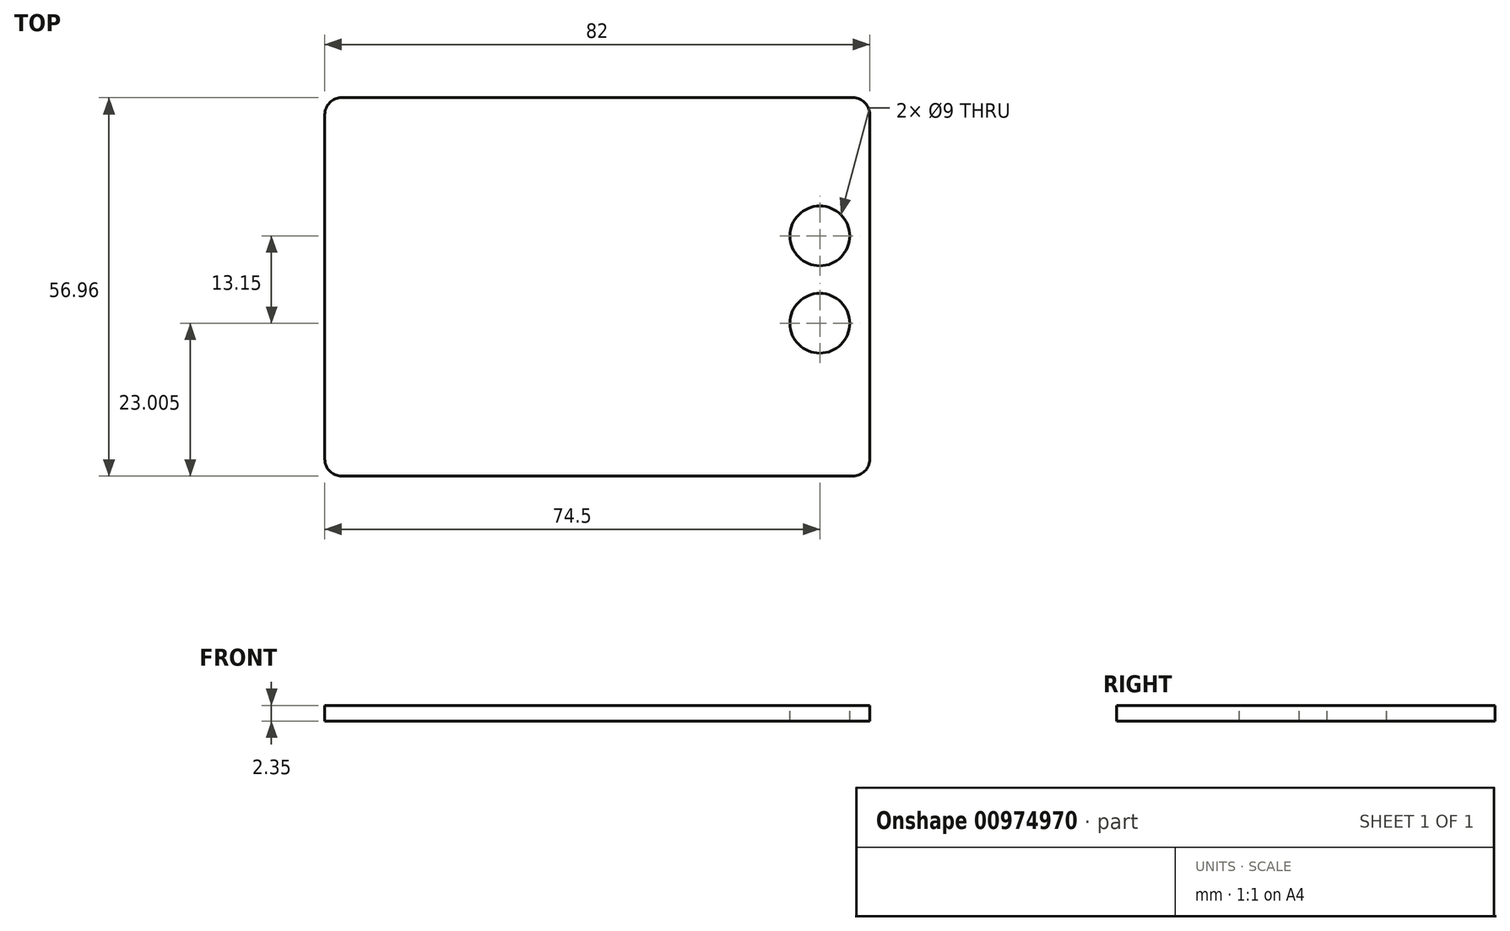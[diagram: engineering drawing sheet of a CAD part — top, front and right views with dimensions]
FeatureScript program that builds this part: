
annotation { "Feature Type Name" : "Feature", "Feature Type Description" : "" }
export const myFeature = defineFeature(function(context is Context, id is Id, definition is map)
    precondition{}
    {
        {
            var Q0;
            Q0=qCreatedBy(makeId("Top.planeOp"),FACE);
            var sketch = newSketch(context, id + "F0", { "sketchPlane" : qUnion([Q0])});
            skLineSegment(sketch, "E0.bottom", {"start": v(-41, 28.47) * mm, "end": v(41, 28.47) * mm});
            skLineSegment(sketch, "E0.top", {"start": v(-41, -28.48) * mm, "end": v(41, -28.48) * mm});
            skLineSegment(sketch, "E0.left", {"start": v(-41, 28.47) * mm, "end": v(-41, -28.47) * mm});
            skLineSegment(sketch, "E0.right", {"start": v(41, 28.47) * mm, "end": v(41, -28.47) * mm});
            skPoint(sketch, "E0.middle", {"position": v(0, 0) * mm});
            skSolve(sketch);
        }
        {
            var Q0;
            Q0 = qSketchRegion(id + "F0", true);
            extrude(context, id + "F1", {"entities" : qUnion([Q0]), "depth" : 2.35 * mm, "offsetDistance" : 25.4 * mm});
        }
        {
            var Q0;
            Q0=makeQuery(id+"F1.opExtrude","SWEPT_EDGE",EDGE,{"disambiguationData":[OSD([sQuery(id+"F0.wireOp",EDGE,"E0.bottom"),sQuery(id+"F0.wireOp",EDGE,"E0.left")])]});
            var Q1;
            Q1=makeQuery(id+"F1.opExtrude","SWEPT_EDGE",EDGE,{"disambiguationData":[OSD([sQuery(id+"F0.wireOp",EDGE,"E0.top"),sQuery(id+"F0.wireOp",EDGE,"E0.left")])]});
            var Q2;
            Q2=makeQuery(id+"F1.opExtrude","SWEPT_EDGE",EDGE,{"disambiguationData":[OSD([sQuery(id+"F0.wireOp",EDGE,"E0.bottom"),sQuery(id+"F0.wireOp",EDGE,"E0.right")])]});
            var Q3;
            Q3=makeQuery(id+"F1.opExtrude","SWEPT_EDGE",EDGE,{"disambiguationData":[OSD([sQuery(id+"F0.wireOp",EDGE,"E0.top"),sQuery(id+"F0.wireOp",EDGE,"E0.right")])]});
            fillet(context, id + "F2", {"entities" : qUnion([Q0, Q1, Q2, Q3]), "radius" : 2.54 * mm, "tangentPropagation" : true, "allowEdgeOverflow" : false});
        }
        {
            var Q0;
            Q0=makeQuery(id+"F1.opExtrude","CAP_FACE",FACE,{"disambiguationData":[OSD([sQuery(id+"F0.wireOp",EDGE,"E0.bottom"),sQuery(id+"F0.wireOp",EDGE,"E0.top"),sQuery(id+"F0.wireOp",EDGE,"E0.left"),sQuery(id+"F0.wireOp",EDGE,"E0.right")])],"isStart":false});
            var sketch = newSketch(context, id + "F3", { "sketchPlane" : qUnion([Q0])});
            skCircle(sketch, "E1", {"center": v(33.5, 7.67) * mm, "radius": 4.5 * mm});
            skLineSegment(sketch, "E2", {"start": v(33.5, 28.47) * mm, "end": v(33.5, 7.67) * mm, "construction": true});
            skLineSegment(sketch, "E3", {"start": v(33.5, 7.67) * mm, "end": v(33.5, -28.48) * mm, "construction": true});
            skCircle(sketch, "E4", {"center": v(33.5, -5.48) * mm, "radius": 4.5 * mm});
            skSolve(sketch);
        }
        {
            var Q0;
            Q0 = qSketchRegion(id + "F3", true);
            extrude(context, id + "F4", {"entities" : qUnion([Q0]), "operationType" : NewBodyOperationType.REMOVE, "endBound" : BoundingType.UP_TO_NEXT, "oppositeDirection" : true, "depth" : 25 * mm, "offsetDistance" : 25 * mm});
        }
    });
